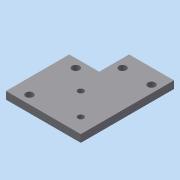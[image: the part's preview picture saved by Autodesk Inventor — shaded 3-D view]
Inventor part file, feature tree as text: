
AUTODESK INVENTOR PART (.ipt)
format: ipt  version: 2015 (Build 190159000, 159)  size: 112,128 bytes
history: native  units: mm
features: sketch x4, other x3
ambient origin geometry x8: Origin, YZ Plane, XZ Plane, XY Plane, X Axis, Y Axis, Z Axis, Center Point
bodies: Solid1 (feature_tree)
feature tree (7):
  other  "Corner mount.ipt"
  other  "Solid1::Corner mount.ipt"
  other  "TaggingFeature1"
  sketch  "Sketch1"  dims[d0=10.0mm]
  sketch  "Sketch2"
  sketch  "Sketch3"
  sketch  "Sketch4"
